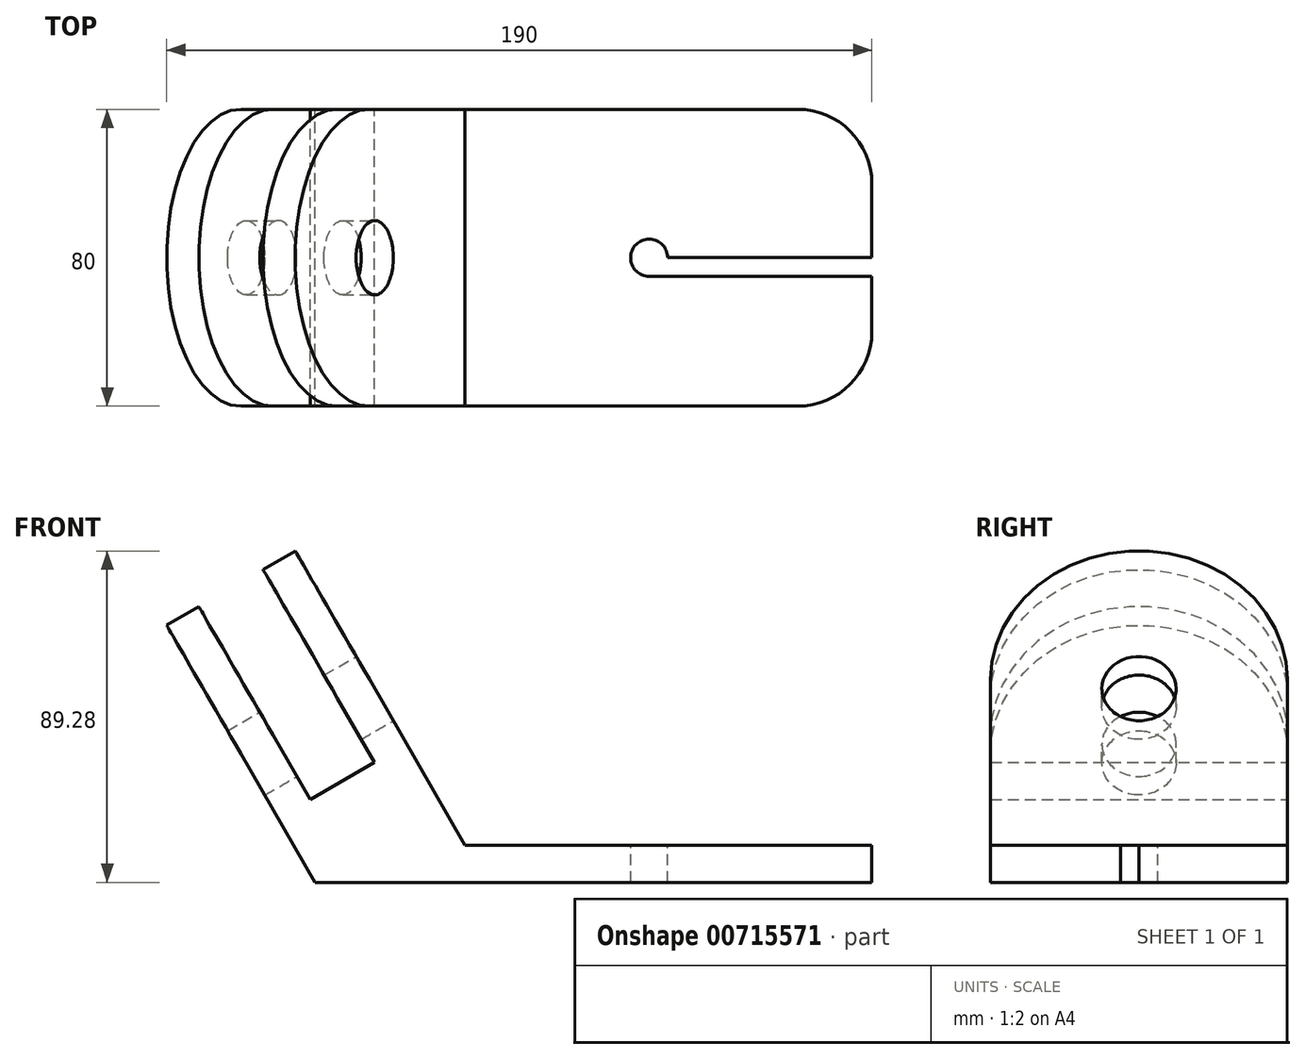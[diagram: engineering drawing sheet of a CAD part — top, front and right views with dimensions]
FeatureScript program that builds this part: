
annotation { "Feature Type Name" : "Feature", "Feature Type Description" : "" }
export const myFeature = defineFeature(function(context is Context, id is Id, definition is map)
    precondition{}
    {
        {
            var Q0;
            Q0=qCreatedBy(makeId("Front.planeOp"),FACE);
            var sketch = newSketch(context, id + "F0", { "sketchPlane" : qUnion([Q0])});
            skLineSegment(sketch, "E0", {"start": v(0, 0) * mm, "end": v(-150, 0) * mm});
            skLineSegment(sketch, "E1", {"start": v(-150, 0) * mm, "end": v(-190, 69.28) * mm});
            skLineSegment(sketch, "E2", {"start": v(-190, 69.28) * mm, "end": v(-181.34, 74.28) * mm});
            skLineSegment(sketch, "E3", {"start": v(-181.34, 74.28) * mm, "end": v(-151.34, 22.32) * mm});
            skLineSegment(sketch, "E4", {"start": v(-151.34, 22.32) * mm, "end": v(-134.02, 32.32) * mm});
            skLineSegment(sketch, "E5", {"start": v(-134.02, 32.32) * mm, "end": v(-164.02, 84.28) * mm});
            skLineSegment(sketch, "E6", {"start": v(-164.02, 84.28) * mm, "end": v(-155.36, 89.28) * mm});
            skLineSegment(sketch, "E7", {"start": v(-155.36, 89.28) * mm, "end": v(-109.59, 10) * mm});
            skLineSegment(sketch, "E8", {"start": v(-109.59, 10) * mm, "end": v(0, 10) * mm});
            skLineSegment(sketch, "E9", {"start": v(0, 10) * mm, "end": v(0, 0) * mm});
            skSolve(sketch);
        }
        {
            var Q0;
            Q0 = qSketchRegion(id + "F0", true);
            extrude(context, id + "F1", {"entities" : qUnion([Q0]), "depth" : 80 * mm, "offsetDistance" : 25 * mm});
        }
        {
            var Q0;
            Q0=makeQuery(id+"F1.opExtrude","CAP_EDGE",EDGE,{"disambiguationData":[OSD([sQuery(id+"F0.wireOp",EDGE,"E6")])],"isStart":false});
            var Q1;
            Q1=makeQuery(id+"F1.opExtrude","CAP_EDGE",EDGE,{"disambiguationData":[OSD([sQuery(id+"F0.wireOp",EDGE,"E6")])],"isStart":true});
            var Q2;
            Q2=makeQuery(id+"F1.opExtrude","CAP_EDGE",EDGE,{"disambiguationData":[OSD([sQuery(id+"F0.wireOp",EDGE,"E2")])],"isStart":false});
            var Q3;
            Q3=makeQuery(id+"F1.opExtrude","CAP_EDGE",EDGE,{"disambiguationData":[OSD([sQuery(id+"F0.wireOp",EDGE,"E2")])],"isStart":true});
            fillet(context, id + "F2", {"entities" : qUnion([Q0, Q1, Q2, Q3]), "radius" : 40 * mm, "tangentPropagation" : true, "allowEdgeOverflow" : false});
        }
        {
            var Q0;
            Q0=makeQuery(id+"F1.opExtrude","SWEPT_FACE",FACE,{"disambiguationData":[OSD([sQuery(id+"F0.wireOp",EDGE,"E7")])]});
            var sketch = newSketch(context, id + "F3", { "sketchPlane" : qUnion([Q0])});
            skLineSegment(sketch, "E10", {"start": v(0, 63.45) * mm, "end": v(0, 112.15) * mm});
            skLineSegment(sketch, "E11", {"start": v(0, 112.15) * mm, "end": v(-40, 112.15) * mm});
            skCircle(sketch, "E12", {"center": v(-40, 112.15) * mm, "radius": 10 * mm});
            skSolve(sketch);
        }
        {
            var Q0;
            Q0 = qSketchRegion(id + "F3", true);
            extrude(context, id + "F4", {"entities" : qUnion([Q0]), "operationType" : NewBodyOperationType.REMOVE, "oppositeDirection" : true, "depth" : 45 * mm, "offsetDistance" : 25 * mm});
        }
        {
            var Q0;
            Q0=makeQuery(id+"F1.opExtrude","SWEPT_FACE",FACE,{"disambiguationData":[OSD([sQuery(id+"F0.wireOp",EDGE,"E8")])]});
            var sketch = newSketch(context, id + "F5", { "sketchPlane" : qUnion([Q0])});
            skLineSegment(sketch, "E13", {"start": v(0, 0) * mm, "end": v(0, -40) * mm});
            skLineSegment(sketch, "E14", {"start": v(0, -40) * mm, "end": v(-60, -40) * mm});
            skCircle(sketch, "E15", {"center": v(-60, -40) * mm, "radius": 5 * mm});
            skLineSegment(sketch, "E16", {"start": v(0, -40) * mm, "end": v(0, -35) * mm});
            skLineSegment(sketch, "E17", {"start": v(0, -40) * mm, "end": v(0, -45) * mm});
            skLineSegment(sketch, "E18", {"start": v(0, -45) * mm, "end": v(-60, -45) * mm});
            skLineSegment(sketch, "E19", {"start": v(0, -35) * mm, "end": v(-60, -35) * mm});
            skSolve(sketch);
        }
        {
            var Q0;
            {var subQ0=sQuery(id+"F5.wireOp",EDGE,"E16");Q0=makeQuery(id+"F5.imprint","IMPRINT",FACE,{"disambiguationData":[TD([[makeQuery(id+"F5.imprint","IMPRINT",EDGE,{"derivedFrom":subQ0}),1.0]])]});}
            var Q1;
            {var subQ0=sQuery(id+"F5.wireOp",EDGE,"E15");var subQ1=makeQuery(id+"F5.imprint","INTERSECT",VERTEX,{"derivedFrom":[subQ0,sQuery(id+"F5.wireOp",EDGE,"E19")]});Q1=makeQuery(id+"F5.imprint","IMPRINT",FACE,{"disambiguationData":[TD([[makeQuery(id+"F5.imprint","IMPRINT",EDGE,{"disambiguationData":[TD([[subQ1,1.0]])],"derivedFrom":subQ0}),1.0]])]});}
            var Q2;
            {var subQ0=sQuery(id+"F5.wireOp",EDGE,"E17");Q2=makeQuery(id+"F5.imprint","IMPRINT",FACE,{"disambiguationData":[TD([[makeQuery(id+"F5.imprint","IMPRINT",EDGE,{"derivedFrom":subQ0}),1.0]])]});}
            extrude(context, id + "F6", {"entities" : qUnion([Q0, Q1, Q2]), "operationType" : NewBodyOperationType.REMOVE, "oppositeDirection" : true, "depth" : 25 * mm, "offsetDistance" : 25 * mm});
        }
        {
            var Q0;
            Q0=makeQuery(id+"F1.opExtrude","CAP_EDGE",EDGE,{"disambiguationData":[OSD([sQuery(id+"F0.wireOp",EDGE,"E9")])],"isStart":false});
            var Q1;
            Q1=makeQuery(id+"F1.opExtrude","CAP_EDGE",EDGE,{"disambiguationData":[OSD([sQuery(id+"F0.wireOp",EDGE,"E9")])],"isStart":true});
            fillet(context, id + "F7", {"entities" : qUnion([Q0, Q1]), "radius" : 20 * mm, "tangentPropagation" : true, "allowEdgeOverflow" : false});
        }
    });
